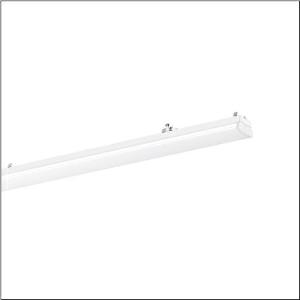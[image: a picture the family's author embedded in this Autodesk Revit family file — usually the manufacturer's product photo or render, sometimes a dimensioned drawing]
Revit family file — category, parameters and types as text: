
# Revit family: licross_r__11_recessed_opal_mo_51tl1d7n46xg_f8f9
name_source: partatom
category: Lighting Fixtures
units: mm (PartAtom-declared; Revit-internal decimal feet)

## family parameters
Cut with Voids When Loaded = No
Host = Face
Light Source = No
Part Type = Normal
Room Calculation Point = No
Round Connector Dimension = Use Diameter
Shared = No

## types (1)
- Licross® 11 recessed opal MO (1 x LED, 6300 lm, 35.1 W, 4000K)
    Apparent Load = 35 VA
    CIE Flux Codes = 44 73 91 87 100
    Color Rendering = 80
    Color Temperature = 4000K
    Default Elevation = 1800 mm
    Description = Licross® 11 recessed opal MO, luminaire insert, of sheet steel, coil coated, white, length: 1.500mm, width: 76mm, height: 87mm, LED rated luminous flux: 6.300lm, light colour: 840, control gear: ON/OFF, with plug, 3-pole, with phase selection, mains connection: 220..240V, AC, 50/60Hz, rated input power: 35W, halogen-free wiring, primary optical cover: cover, of PMMA, light emission: direct with ceiling illumination distribution, primary light characteristic: symmetric, protection rating (complete): IP40, insulation class (complete): insulation class I (protective earthing), certification: CE, ENEC, VDE, UKCA, protection symbol: D if used in an environment without relevant dust loads with corresponding accessories, impact resistance: IK06, permissible ambient temperature for indoor applications: -35..+45°C, corresponds to IFS (International Featured Standards) requirements for safety and quality in the food industry, reducing of maximum allowable ambient temperature of 5°C with ceiling mounting, packaging unit: 1 piece
    Height = 83 mm
    Lamp = 1 x LED
    Lamp Light Flux = 6300 lm
    Lamp Power = 35.1 W
    Lamp count = 1
    Length = 1500 mm
    Luminous efficacy = 179 lm/W
    Manufacturer = Siteco
    ModVariant = No
    Model = 51TL1D7N46XG
    Mounting Place = Ceiling
    Mounting Type = Pendant
    Number of Poles = 1
    OnlyDefault = Yes
    Power Factor = 1
    Product Name = Licross® 11 recessed opal MO
    Product group = luminaire insert
    ProductGroupID = 901
    Protection Class = Protection class I
    Protection Degree = IP 40
    RLX_Detail_Level = 1
    RLX_Emergency_Light_Flux = 0 lm
    RLX_Emergency_Type = 0
    RLX_Emergency_Type_DB = No
    RlxData = <blob elided: 23041 chars, md5=2d98b616>
    Socket = socket
    Standby Power = 0 W
    System Light Flux = 6300 lm
    System Power = 35 W
    Type Comments = Product without accessories
    Type Image = l_1313666.jpg
    URL = http://relux.com
    VarID = ---
    Voltage = 0 V
    Weight = 0.00 kg
    Width = 76 mm

## geometry (parser evidence)
native form markers: Blend x4, Sweep x13
no freeform markers — native parametric forms only
